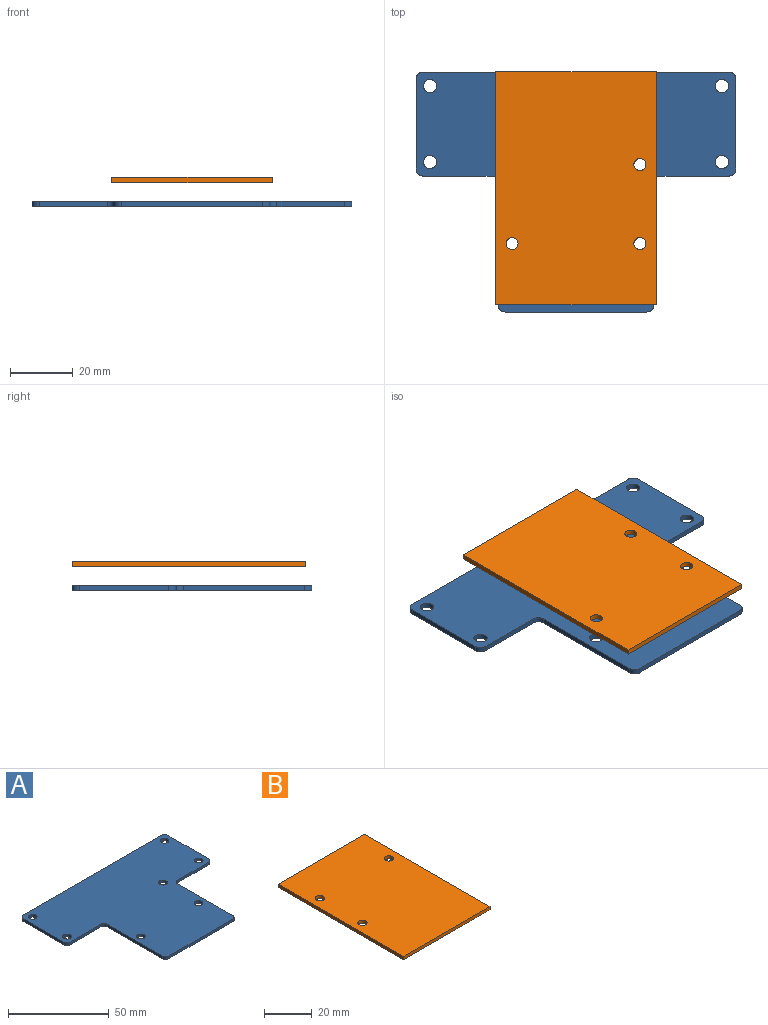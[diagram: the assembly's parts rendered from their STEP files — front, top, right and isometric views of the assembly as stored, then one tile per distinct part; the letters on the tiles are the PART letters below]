
ASSEMBLY  parts=2 mates=1
PART A: 25 faces, bbox 101.6x76.2x1.6 mm
  f0: plane 28.55x1.6mm, normal (-1,0,0), area 45.7mm2, adj f15,f16,f17,f24
  f1: plane 21.59x1.6mm, normal (0,-1,0), area 34.5mm2, adj f15,f16,f17,f18
  f2: plane 38.71x1.6mm, normal (-1,0,0), area 61.9mm2, adj f15,f16,f18,f19
  f3: plane 45.01x1.6mm, normal (0,-1,0), area 72mm2, adj f15,f16,f19,f20
  f4: plane 38.71x1.6mm, normal (1,0,0), area 61.9mm2, adj f15,f16,f20,f21
  f5: plane 21.59x1.6mm, normal (0,-1,0), area 34.5mm2, adj f15,f16,f21,f22
  f6: plane 28.55x1.6mm, normal (1,0,0), area 45.7mm2, adj f15,f16,f22,f23
  f7: cylinder r=2.11mm len=4.22mm, axis (0,0,-1), area 21.2mm2, adj f15,f16
  f8: cylinder r=2.11mm len=4.22mm, axis (0,0,-1), area 21.2mm2, adj f15,f16
  f9: cylinder r=2.11mm len=4.22mm, axis (0,0,-1), area 21.2mm2, adj f15,f16
  f10: cylinder r=2.11mm len=4.22mm, axis (0,0,-1), area 21.2mm2, adj f15,f16
  f11: cylinder r=2.11mm len=4.22mm, axis (0,0,-1), area 21.2mm2, adj f15,f16
  f12: cylinder r=2.11mm len=4.22mm, axis (0,0,-1), area 21.2mm2, adj f15,f16
  f13: cylinder r=2.11mm len=4.22mm, axis (0,0,-1), area 21.2mm2, adj f15,f16
  f14: plane 97.13x1.6mm, normal (0,1,0), area 155.4mm2, adj f15,f16,f23,f24
  f15: plane 101.6x76.2mm, normal (0,0,1), area 5389.3mm2, adj f0,f1,f2,f3,f4,f5,f6,f7
  f16: plane 101.6x76.2mm, normal (0,0,-1), area 5389.3mm2, adj f0,f1,f2,f3,f4,f5,f6,f7
  f17: cylinder r=2.24mm len=2.24mm, axis (0,0,-1), area 5.6mm2, adj f0,f1,f15,f16
  f18: cylinder r=2.24mm len=2.24mm, axis (0,0,-1), area 5.6mm2, adj f1,f2,f15,f16
  f19: cylinder r=2.24mm len=2.24mm, axis (0,0,1), area 5.6mm2, adj f2,f3,f15,f16
  f20: cylinder r=2.24mm len=2.24mm, axis (0,0,-1), area 5.6mm2, adj f3,f4,f15,f16
  f21: cylinder r=2.24mm len=2.24mm, axis (0,0,1), area 5.6mm2, adj f4,f5,f15,f16
  f22: cylinder r=2.24mm len=2.24mm, axis (0,0,1), area 5.6mm2, adj f5,f6,f15,f16
  f23: cylinder r=2.24mm len=2.24mm, axis (0,0,-1), area 5.6mm2, adj f6,f14,f15,f16
  f24: cylinder r=2.24mm len=2.24mm, axis (0,0,1), area 5.6mm2, adj f0,f14,f15,f16
PART B: 9 faces, bbox 51x74x1.6 mm
  f0: plane 51x1.6mm, normal (0,1,0), area 81.6mm2, adj f1,f6,f7,f8
  f1: plane 74x1.6mm, normal (-1,0,0), area 118.4mm2, adj f0,f2,f7,f8
  f2: plane 51x1.6mm, normal (0,-1,0), area 81.6mm2, adj f1,f6,f7,f8
  f3: cylinder r=1.91mm len=3.81mm, axis (0,0,-1), area 19.2mm2, adj f7,f8
  f4: cylinder r=1.91mm len=3.81mm, axis (0,0,-1), area 19.2mm2, adj f7,f8
  f5: cylinder r=1.91mm len=3.81mm, axis (0,0,-1), area 19.2mm2, adj f7,f8
  f6: plane 74x1.6mm, normal (1,0,0), area 118.4mm2, adj f0,f2,f7,f8
  f7: plane 74x51mm, normal (0,0,1), area 3739.8mm2, adj f0,f1,f2,f3,f4,f5,f6
  f8: plane 74x51mm, normal (0,0,-1), area 3739.8mm2, adj f0,f1,f2,f3,f4,f5,f6
PLACE A rot(axis=(-1,-0.07,0.02),0deg) t=(-17.79,-14.49,16.67)mm
PLACE B rot(axis=(0,0,-1),180deg) t=(54.58,-150.34,24.29)mm
MATE cylindrical A.f13 <-> B.f4  axis (0,0,1) through (-36.15,-20.51,18.27)mm
